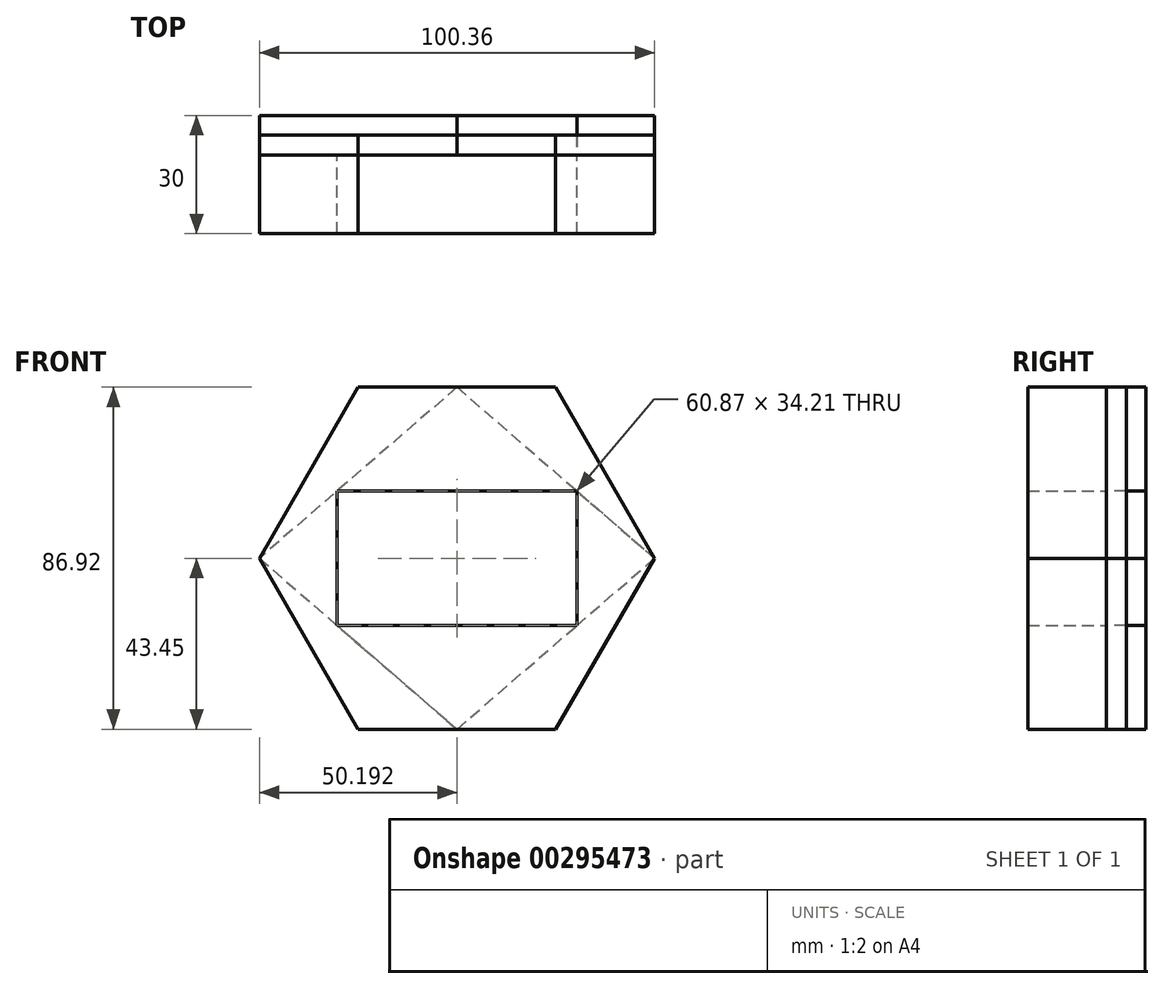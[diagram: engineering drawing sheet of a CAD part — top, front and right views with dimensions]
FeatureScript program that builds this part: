
annotation { "Feature Type Name" : "Feature", "Feature Type Description" : "" }
export const myFeature = defineFeature(function(context is Context, id is Id, definition is map)
    precondition{}
    {
        {
            var Q0;
            Q0=qCreatedBy(makeId("Front.planeOp"),FACE);
            var sketch = newSketch(context, id + "F0", { "sketchPlane" : qUnion([Q0])});
            skLineSegment(sketch, "E0.0", {"start": v(-25.1, 43.46) * mm, "end": v(25.1, 43.46) * mm});
            skLineSegment(sketch, "E0.1", {"start": v(25.1, 43.46) * mm, "end": v(50.18, 0) * mm});
            skLineSegment(sketch, "E0.2", {"start": v(50.18, 0) * mm, "end": v(25.1, -43.46) * mm});
            skLineSegment(sketch, "E0.3", {"start": v(25.1, -43.46) * mm, "end": v(-25.1, -43.46) * mm});
            skLineSegment(sketch, "E0.4", {"start": v(-25.1, -43.46) * mm, "end": v(-50.18, 0) * mm});
            skLineSegment(sketch, "E0.5", {"start": v(-50.18, 0) * mm, "end": v(-25.1, 43.46) * mm});
            skPoint(sketch, "E0.0.midPoint", {"position": v(0, 43.46) * mm});
            skLineSegment(sketch, "E1", {"start": v(0, 43.46) * mm, "end": v(-50.18, 0) * mm});
            skLineSegment(sketch, "E2", {"start": v(-50.18, 0) * mm, "end": v(0, -43.46) * mm});
            skLineSegment(sketch, "E3", {"start": v(0, -43.46) * mm, "end": v(50.18, 0) * mm});
            skLineSegment(sketch, "E4", {"start": v(0, 43.46) * mm, "end": v(50.18, 0) * mm});
            skLineSegment(sketch, "E5.bottom", {"start": v(-30.42, -17.11) * mm, "end": v(30.45, -17.11) * mm});
            skLineSegment(sketch, "E5.top", {"start": v(-30.42, 17.1) * mm, "end": v(30.45, 17.1) * mm});
            skLineSegment(sketch, "E5.left", {"start": v(-30.42, -17.11) * mm, "end": v(-30.42, 17.1) * mm});
            skLineSegment(sketch, "E5.right", {"start": v(30.45, -17.11) * mm, "end": v(30.45, 17.1) * mm});
            skPoint(sketch, "E0.cCircle.center.orphan", {"position": v(0, 0) * mm});
            skSolve(sketch);
        }
        {
            var Q0;
            {var subQ1=sQuery(id+"F0.wireOp",EDGE,"E1");Q0=makeQuery(id+"F0.imprint","IMPRINT",FACE,{"disambiguationData":[TD([[makeQuery(id+"F0.imprint","IMPRINT",EDGE,{"derivedFrom":subQ1}),1.0]])]});}
            var Q1;
            {var subQ0=sQuery(id+"F0.wireOp",EDGE,"E0.5");Q1=makeQuery(id+"F0.imprint","IMPRINT",FACE,{"disambiguationData":[TD([[makeQuery(id+"F0.imprint","IMPRINT",EDGE,{"derivedFrom":subQ0}),-1.0]])]});}
            var Q2;
            {var subQ0=sQuery(id+"F0.wireOp",EDGE,"E0.1");Q2=makeQuery(id+"F0.imprint","IMPRINT",FACE,{"disambiguationData":[TD([[makeQuery(id+"F0.imprint","IMPRINT",EDGE,{"derivedFrom":subQ0}),-1.0]])]});}
            var Q3;
            {var subQ1=sQuery(id+"F0.wireOp",EDGE,"E3");var subQ3=sQuery(id+"F0.wireOp",EDGE,"E5.right");var subQ4=makeQuery(id+"F0.imprint","INTERSECT",VERTEX,{"derivedFrom":[subQ1,subQ3]});Q3=makeQuery(id+"F0.imprint","IMPRINT",FACE,{"disambiguationData":[TD([[makeQuery(id+"F0.imprint","IMPRINT",EDGE,{"disambiguationData":[TD([[subQ4,-1.0]])],"derivedFrom":subQ3}),-1.0]])]});}
            var Q4;
            {var subQ5=sQuery(id+"F0.wireOp",EDGE,"E0.2");Q4=makeQuery(id+"F0.imprint","IMPRINT",FACE,{"disambiguationData":[TD([[makeQuery(id+"F0.imprint","IMPRINT",EDGE,{"derivedFrom":subQ5}),-1.0]])]});}
            var Q5;
            {var subQ0=sQuery(id+"F0.wireOp",EDGE,"E0.4");Q5=makeQuery(id+"F0.imprint","IMPRINT",FACE,{"disambiguationData":[TD([[makeQuery(id+"F0.imprint","IMPRINT",EDGE,{"derivedFrom":subQ0}),-1.0]])]});}
            var Q6;
            {var subQ0=sQuery(id+"F0.wireOp",EDGE,"E3");var subQ3=sQuery(id+"F0.wireOp",EDGE,"E5.bottom");var subQ5=makeQuery(id+"F0.imprint","INTERSECT",VERTEX,{"derivedFrom":[subQ0,subQ3]});Q6=makeQuery(id+"F0.imprint","IMPRINT",FACE,{"disambiguationData":[TD([[makeQuery(id+"F0.imprint","IMPRINT",EDGE,{"disambiguationData":[TD([[subQ5,1.0]])],"derivedFrom":subQ0}),1.0]])]});}
            extrude(context, id + "F1", {"entities" : qUnion([Q0, Q1, Q2, Q3, Q4, Q5, Q6]), "depth" : 20 * mm});
        }
        {
            var Q0;
            {var subQ0=sQuery(id+"F0.wireOp",EDGE,"E3");var subQ3=sQuery(id+"F0.wireOp",EDGE,"E5.bottom");var subQ5=makeQuery(id+"F0.imprint","INTERSECT",VERTEX,{"derivedFrom":[subQ0,subQ3]});Q0=makeQuery(id+"F0.imprint","IMPRINT",FACE,{"disambiguationData":[TD([[makeQuery(id+"F0.imprint","IMPRINT",EDGE,{"disambiguationData":[TD([[subQ5,1.0]])],"derivedFrom":subQ0}),1.0]])]});}
            var Q1;
            {var subQ1=sQuery(id+"F0.wireOp",EDGE,"E3");var subQ3=sQuery(id+"F0.wireOp",EDGE,"E5.right");var subQ4=makeQuery(id+"F0.imprint","INTERSECT",VERTEX,{"derivedFrom":[subQ1,subQ3]});Q1=makeQuery(id+"F0.imprint","IMPRINT",FACE,{"disambiguationData":[TD([[makeQuery(id+"F0.imprint","IMPRINT",EDGE,{"disambiguationData":[TD([[subQ4,-1.0]])],"derivedFrom":subQ3}),-1.0]])]});}
            var Q2;
            {var subQ1=sQuery(id+"F0.wireOp",EDGE,"E1");Q2=makeQuery(id+"F0.imprint","IMPRINT",FACE,{"disambiguationData":[TD([[makeQuery(id+"F0.imprint","IMPRINT",EDGE,{"derivedFrom":subQ1}),1.0]])]});}
            extrude(context, id + "F2", {"entities" : qUnion([Q0, Q1, Q2]), "oppositeDirection" : true, "depth" : 10 * mm});
        }
        {
            var Q0;
            {var subQ0=sQuery(id+"F0.wireOp",EDGE,"E0.5");Q0=makeQuery(id+"F0.imprint","IMPRINT",FACE,{"disambiguationData":[TD([[makeQuery(id+"F0.imprint","IMPRINT",EDGE,{"derivedFrom":subQ0}),-1.0]])]});}
            var Q1;
            {var subQ0=sQuery(id+"F0.wireOp",EDGE,"E0.1");Q1=makeQuery(id+"F0.imprint","IMPRINT",FACE,{"disambiguationData":[TD([[makeQuery(id+"F0.imprint","IMPRINT",EDGE,{"derivedFrom":subQ0}),-1.0]])]});}
            var Q2;
            {var subQ0=sQuery(id+"F0.wireOp",EDGE,"E0.4");Q2=makeQuery(id+"F0.imprint","IMPRINT",FACE,{"disambiguationData":[TD([[makeQuery(id+"F0.imprint","IMPRINT",EDGE,{"derivedFrom":subQ0}),-1.0]])]});}
            var Q3;
            {var subQ5=sQuery(id+"F0.wireOp",EDGE,"E0.2");Q3=makeQuery(id+"F0.imprint","IMPRINT",FACE,{"disambiguationData":[TD([[makeQuery(id+"F0.imprint","IMPRINT",EDGE,{"derivedFrom":subQ5}),-1.0]])]});}
            extrude(context, id + "F3", {"entities" : qUnion([Q0, Q1, Q2, Q3]), "oppositeDirection" : true, "depth" : 5 * mm});
        }
    });
